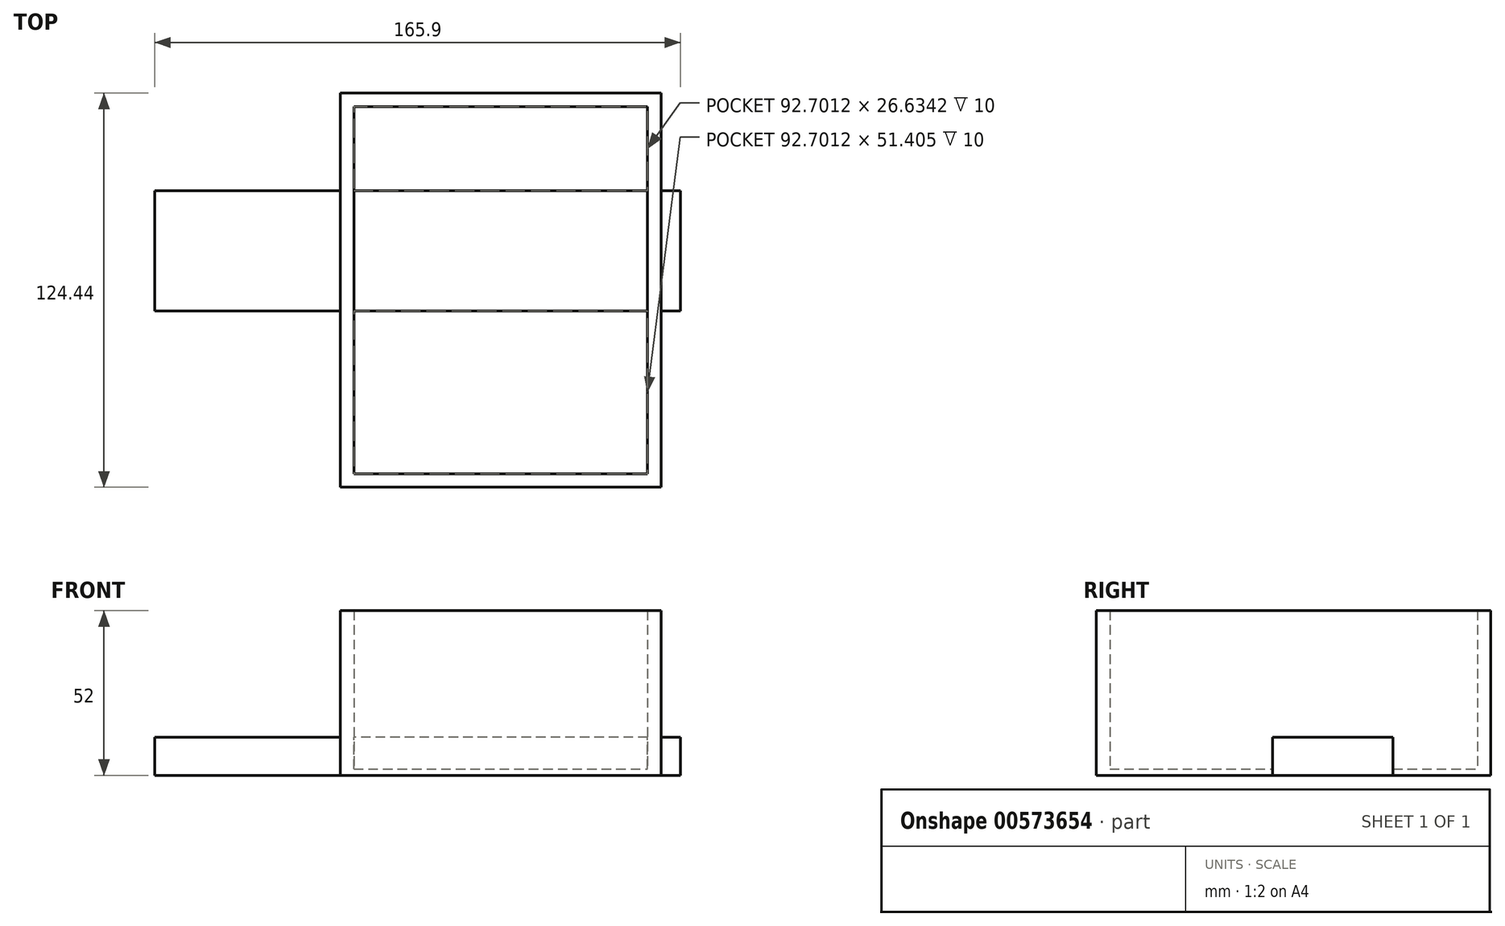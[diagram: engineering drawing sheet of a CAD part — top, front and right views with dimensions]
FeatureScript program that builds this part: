
annotation { "Feature Type Name" : "Feature", "Feature Type Description" : "" }
export const myFeature = defineFeature(function(context is Context, id is Id, definition is map)
    precondition{}
    {
        {
            var Q0;
            Q0=qCreatedBy(makeId("Top.planeOp"),FACE);
            var sketch = newSketch(context, id + "F0", { "sketchPlane" : qUnion([Q0])});
            skLineSegment(sketch, "E0.bottom", {"start": v(50.58, -62.22) * mm, "end": v(-50.58, -62.22) * mm});
            skLineSegment(sketch, "E0.top", {"start": v(50.58, 62.22) * mm, "end": v(-50.58, 62.22) * mm});
            skLineSegment(sketch, "E0.left", {"start": v(50.58, -62.22) * mm, "end": v(50.58, 62.22) * mm});
            skLineSegment(sketch, "E0.right", {"start": v(-50.58, -62.22) * mm, "end": v(-50.58, 62.22) * mm});
            skPoint(sketch, "E0.middle", {"position": v(0, 0) * mm});
            skSolve(sketch);
        }
        {
            var Q0;
            Q0 = qSketchRegion(id + "F0", true);
            extrude(context, id + "F1", {"entities" : qUnion([Q0]), "depth" : 2 * mm, "offsetDistance" : 25 * mm});
        }
        {
            var Q0;
            Q0=makeQuery(id+"F1.opExtrude","CAP_FACE",FACE,{"disambiguationData":[OSD([sQuery(id+"F0.wireOp",EDGE,"E0.bottom"),sQuery(id+"F0.wireOp",EDGE,"E0.top"),sQuery(id+"F0.wireOp",EDGE,"E0.left"),sQuery(id+"F0.wireOp",EDGE,"E0.right")])],"isStart":false});
            var sketch = newSketch(context, id + "F2", { "sketchPlane" : qUnion([Q0])});
            skLineSegment(sketch, "E1.bottom", {"start": v(50.58, -62.22) * mm, "end": v(-50.58, -62.22) * mm});
            skLineSegment(sketch, "E1.top", {"start": v(50.58, 62.22) * mm, "end": v(-50.58, 62.22) * mm});
            skLineSegment(sketch, "E1.left", {"start": v(50.58, -62.22) * mm, "end": v(50.58, 62.22) * mm});
            skLineSegment(sketch, "E1.right", {"start": v(-50.58, -62.22) * mm, "end": v(-50.58, 62.22) * mm});
            skPoint(sketch, "E1.middle", {"position": v(0, 0) * mm});
            skLineSegment(sketch, "E2.bottom", {"start": v(46.35, -57.99) * mm, "end": v(-46.35, -57.99) * mm});
            skLineSegment(sketch, "E2.top", {"start": v(46.35, 57.99) * mm, "end": v(-46.35, 57.99) * mm});
            skLineSegment(sketch, "E2.left", {"start": v(46.35, -57.99) * mm, "end": v(46.35, 57.99) * mm});
            skLineSegment(sketch, "E2.right", {"start": v(-46.35, -57.99) * mm, "end": v(-46.35, 57.99) * mm});
            skSolve(sketch);
        }
        {
            var Q0;
            Q0 = qSketchRegion(id + "F2", true);
            extrude(context, id + "F3", {"entities" : qUnion([Q0]), "operationType" : NewBodyOperationType.ADD, "depth" : 50 * mm, "offsetDistance" : 25 * mm});
        }
        {
            var Q0;
            Q0=qCreatedBy(makeId("Top.planeOp"),FACE);
            var sketch = newSketch(context, id + "F4", { "sketchPlane" : qUnion([Q0])});
            skLineSegment(sketch, "E3.bottom", {"start": v(56.73, -6.58) * mm, "end": v(-109.17, -6.58) * mm});
            skLineSegment(sketch, "E3.top", {"start": v(56.73, 31.36) * mm, "end": v(-109.17, 31.36) * mm});
            skLineSegment(sketch, "E3.left", {"start": v(56.73, -6.58) * mm, "end": v(56.73, 31.36) * mm});
            skLineSegment(sketch, "E3.right", {"start": v(-109.17, -6.58) * mm, "end": v(-109.17, 31.36) * mm});
            skPoint(sketch, "E3.middle", {"position": v(-26.22, 12.39) * mm});
            skSolve(sketch);
        }
        {
            var Q0;
            Q0 = qSketchRegion(id + "F4", true);
            extrude(context, id + "F5", {"entities" : qUnion([Q0]), "operationType" : NewBodyOperationType.ADD, "depth" : 12 * mm, "offsetDistance" : 25 * mm});
        }
    });
